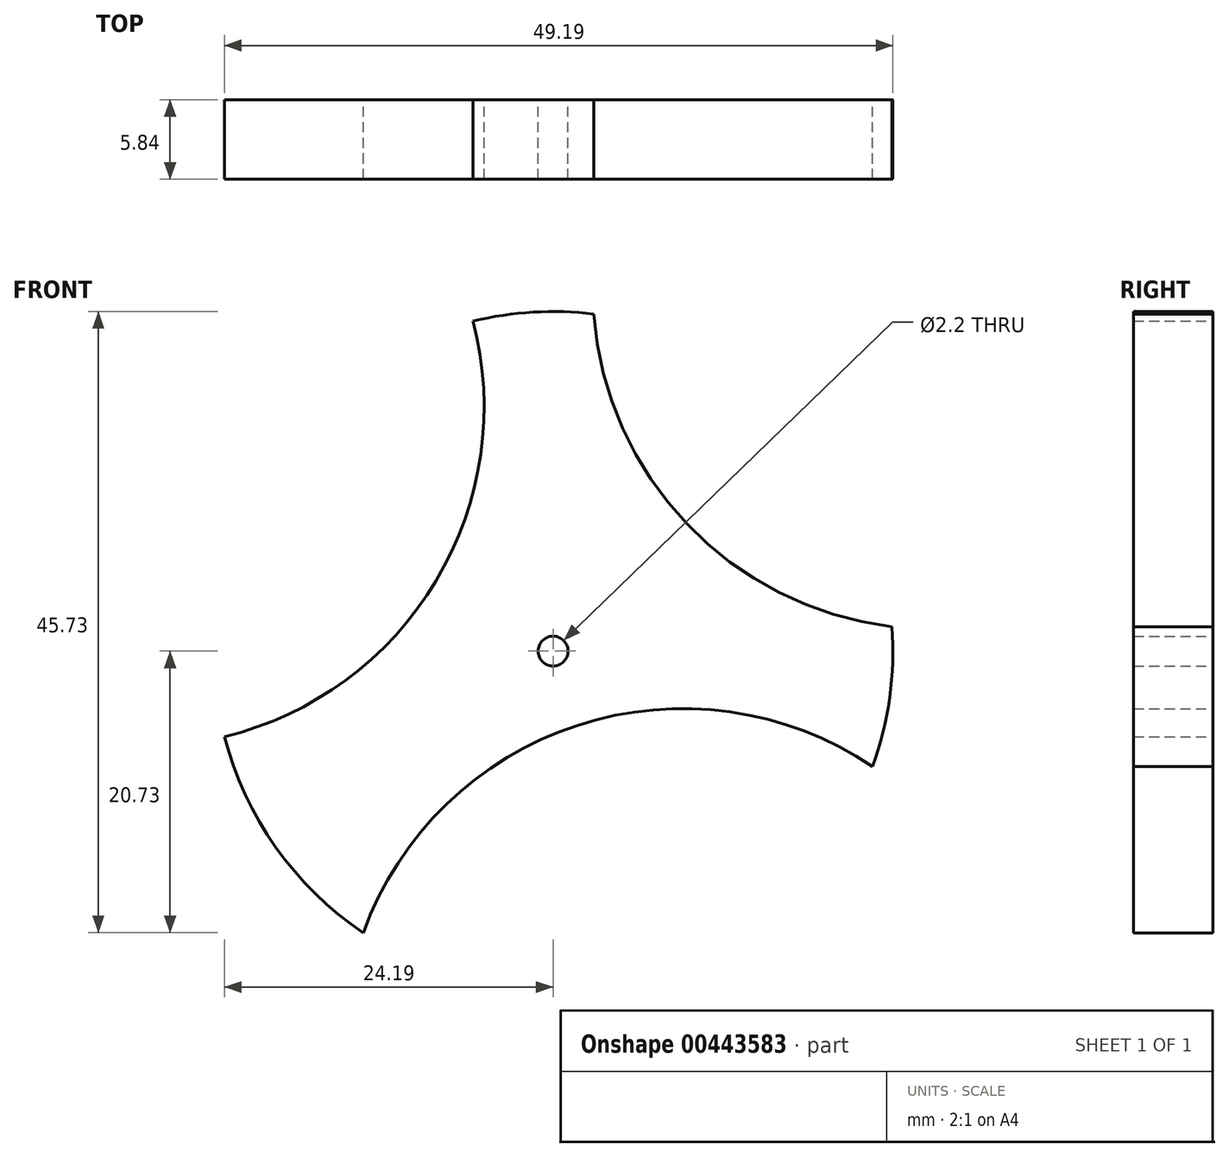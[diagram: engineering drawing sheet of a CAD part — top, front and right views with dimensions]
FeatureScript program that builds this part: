
annotation { "Feature Type Name" : "Feature", "Feature Type Description" : "" }
export const myFeature = defineFeature(function(context is Context, id is Id, definition is map)
    precondition{}
    {
        {
            var Q0;
            Q0=qCreatedBy(makeId("Front.planeOp"),FACE);
            var sketch = newSketch(context, id + "F0", { "sketchPlane" : qUnion([Q0])});
            skCircle(sketch, "E0", {"center": v(0, 0) * mm, "radius": 25 * mm});
            skCircle(sketch, "E1", {"center": v(0, 0) * mm, "radius": 1.1 * mm});
            skCircle(sketch, "E2", {"center": v(-30.08, 18) * mm, "radius": 25 * mm});
            skCircle(sketch, "E3", {"center": v(9.55, -29.23) * mm, "radius": 25 * mm});
            skCircle(sketch, "E4", {"center": v(27.93, 26.62) * mm, "radius": 25 * mm});
            skSolve(sketch);
        }
        {
            var Q0;
            Q0=makeQuery(id+"F0.imprint","IMPRINT",FACE,{"disambiguationData":[TD([[makeQuery(id+"F0.imprint","IMPRINT",EDGE,{"derivedFrom":sQuery(id+"F0.wireOp",EDGE,"E1")}),-1.0]])]});
            extrude(context, id + "F1", {"entities" : qUnion([Q0]), "depth" : 5.84 * mm});
        }
    });
